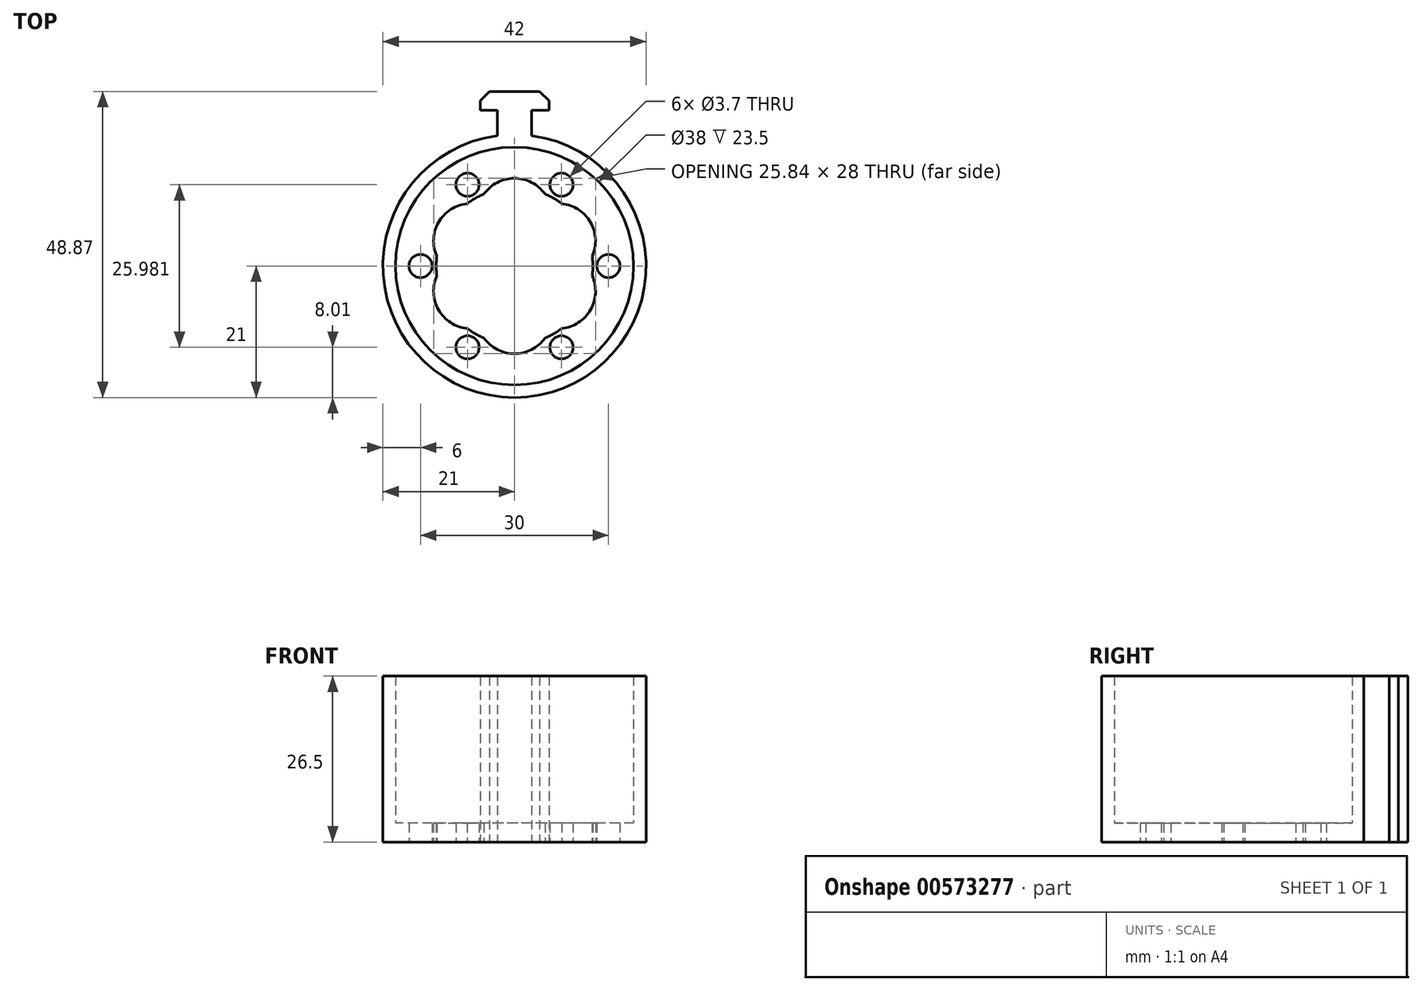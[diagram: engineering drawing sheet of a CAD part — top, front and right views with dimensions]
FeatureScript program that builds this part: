
annotation { "Feature Type Name" : "Feature", "Feature Type Description" : "" }
export const myFeature = defineFeature(function(context is Context, id is Id, definition is map)
    precondition{}
    {
        {
            var Q0;
            Q0=qCreatedBy(makeId("Top.planeOp"),FACE);
            var sketch = newSketch(context, id + "F0", { "sketchPlane" : qUnion([Q0])});
            skCircle(sketch, "E0", {"center": v(0, 0) * mm, "radius": 19 * mm});
            skCircle(sketch, "E1", {"center": v(0, 0) * mm, "radius": 12.5 * mm});
            skLineSegment(sketch, "E2", {"start": v(0, 0) * mm, "end": v(0, 21.75) * mm});
            skCircle(sketch, "E3", {"center": v(0, 8) * mm, "radius": 6 * mm});
            skCircle(sketch, "E4.1.0", {"center": v(-6.93, 4) * mm, "radius": 6 * mm});
            skCircle(sketch, "E4.2.0", {"center": v(-6.93, -4) * mm, "radius": 6 * mm});
            skCircle(sketch, "E4.3.0", {"center": v(0, -8) * mm, "radius": 6 * mm});
            skCircle(sketch, "E4.4.0", {"center": v(6.93, -4) * mm, "radius": 6 * mm});
            skCircle(sketch, "E4.5.0", {"center": v(6.93, 4) * mm, "radius": 6 * mm});
            skCircle(sketch, "E5", {"center": v(-15, 0) * mm, "radius": 1.85 * mm});
            skCircle(sketch, "E6.1.0", {"center": v(-7.5, -13) * mm, "radius": 1.85 * mm});
            skCircle(sketch, "E6.2.0", {"center": v(7.5, -13) * mm, "radius": 1.85 * mm});
            skCircle(sketch, "E6.3.0", {"center": v(15, 0) * mm, "radius": 1.85 * mm});
            skCircle(sketch, "E6.4.0", {"center": v(7.5, 13) * mm, "radius": 1.85 * mm});
            skCircle(sketch, "E6.5.0", {"center": v(-7.5, 13) * mm, "radius": 1.85 * mm});
            skSolve(sketch);
        }
        {
            var Q0;
            Q0 = qSketchRegion(id + "F0", true);
            extrude(context, id + "F1", {"entities" : qUnion([Q0]), "depth" : 3 * mm, "offsetDistance" : 25 * mm});
        }
        {
            var Q0;
            Q0=qCreatedBy(makeId("Top.planeOp"),FACE);
            var sketch = newSketch(context, id + "F2", { "sketchPlane" : qUnion([Q0])});
            skCircle(sketch, "E7", {"center": v(0, 0) * mm, "radius": 19 * mm});
            skCircle(sketch, "E8", {"center": v(0, 0) * mm, "radius": 21 * mm});
            skLineSegment(sketch, "E9", {"start": v(0, 24.87) * mm, "end": v(-3.4, 24.87) * mm});
            skLineSegment(sketch, "E10", {"start": v(0, 24.87) * mm, "end": v(-5.5, 24.87) * mm});
            skLineSegment(sketch, "E11", {"start": v(0, 24.87) * mm, "end": v(0, 27.87) * mm});
            skLineSegment(sketch, "E12", {"start": v(0, 27.87) * mm, "end": v(4, 27.87) * mm});
            skLineSegment(sketch, "E13", {"start": v(0, 27.87) * mm, "end": v(-4, 27.87) * mm});
            skLineSegment(sketch, "E14", {"start": v(0, 24.87) * mm, "end": v(5.5, 24.87) * mm});
            skLineSegment(sketch, "E15", {"start": v(5.5, 24.87) * mm, "end": v(5.5, 26.37) * mm});
            skLineSegment(sketch, "E16", {"start": v(5.5, 26.37) * mm, "end": v(4, 27.87) * mm});
            skLineSegment(sketch, "E17", {"start": v(-5.5, 24.87) * mm, "end": v(-5.5, 26.37) * mm});
            skLineSegment(sketch, "E18", {"start": v(-5.5, 26.37) * mm, "end": v(-4, 27.87) * mm});
            skLineSegment(sketch, "E19", {"start": v(0, 24.87) * mm, "end": v(-2.74, 24.87) * mm});
            skLineSegment(sketch, "E20", {"start": v(-2.74, 24.87) * mm, "end": v(-2.74, 20.82) * mm});
            skLineSegment(sketch, "E21", {"start": v(0, 24.87) * mm, "end": v(2.76, 24.87) * mm});
            skLineSegment(sketch, "E22", {"start": v(2.76, 24.87) * mm, "end": v(2.76, 20.82) * mm});
            skSolve(sketch);
        }
        {
            var Q0;
            Q0 = qSketchRegion(id + "F2", true);
            extrude(context, id + "F3", {"entities" : qUnion([Q0]), "operationType" : NewBodyOperationType.ADD, "depth" : 26.5 * mm, "offsetDistance" : 25 * mm});
        }
    });
